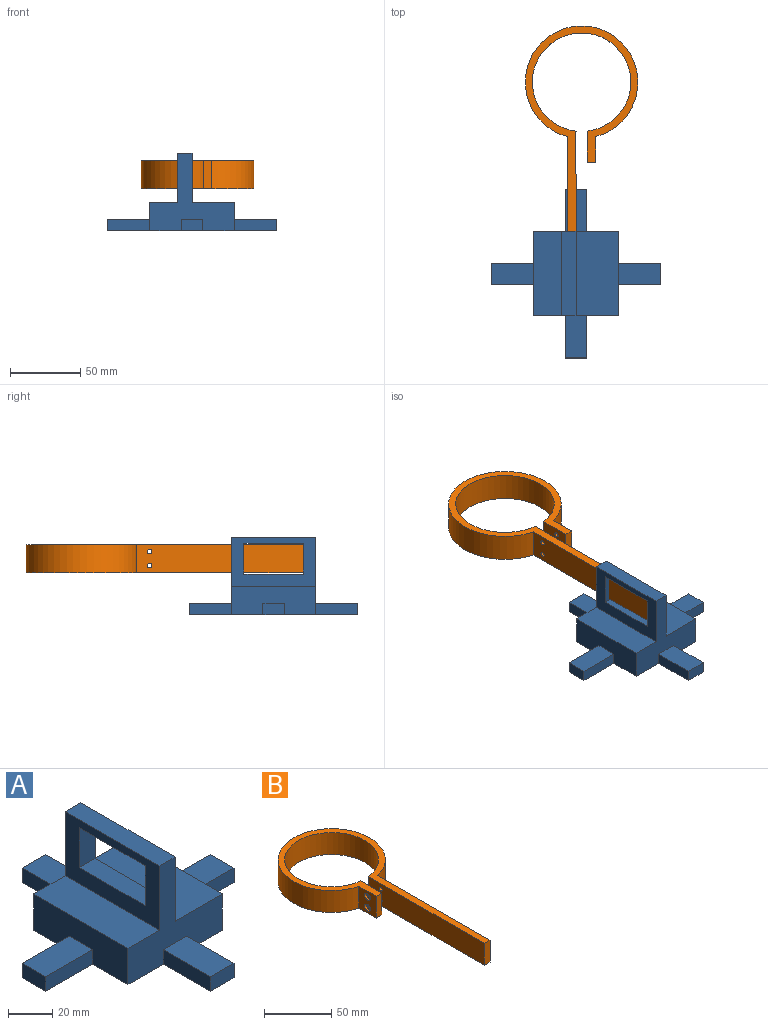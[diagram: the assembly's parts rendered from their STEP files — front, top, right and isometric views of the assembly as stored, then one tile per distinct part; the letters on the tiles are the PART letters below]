
ASSEMBLY  parts=2 mates=1
PART A: 30 faces, bbox 120x120x55.3 mm
  f0: plane 60x35.32mm, normal (-1,0,0), area 1195.5mm2, adj f4,f5,f7,f25,f26,f27,f28,f29
  f1: plane 60x35.32mm, normal (1,0,0), area 1195.5mm2, adj f2,f4,f5,f25,f26,f27,f28,f29
  f2: plane 60x30mm, normal (0,0,1), area 1800mm2, adj f1,f4,f5,f6
  f3: plane 60x20mm, normal (-1,0,0), area 1080mm2, adj f4,f5,f7,f8,f21,f23,f24
  f4: plane 60x55.32mm, normal (0,1,0), area 1433.2mm2, adj f0,f1,f2,f3,f6,f7,f8,f9
  f5: plane 60x55.32mm, normal (0,-1,0), area 1433.2mm2, adj f0,f1,f2,f3,f6,f7,f8,f13
  f6: plane 60x20mm, normal (1,0,0), area 1080mm2, adj f2,f4,f5,f8,f17,f18,f20
  f7: plane 60x20mm, normal (0,0,1), area 1200mm2, adj f0,f3,f4,f5
  f8: plane 120x120mm, normal (0,0,-1), area 5400mm2, adj f3,f4,f5,f6,f9,f10,f11,f13
  f9: plane 30x8mm, normal (-1,0,0), area 240mm2, adj f4,f8,f11,f12
  f10: plane 30x8mm, normal (1,0,0), area 240mm2, adj f4,f8,f11,f12
  f11: plane 15x8mm, normal (0,1,0), area 120mm2, adj f8,f9,f10,f12
  f12: plane 30x15mm, normal (0,0,1), area 450mm2, adj f4,f9,f10,f11
  f13: plane 30x8mm, normal (1,0,0), area 240mm2, adj f5,f8,f15,f16
  f14: plane 30x8mm, normal (-1,0,0), area 240mm2, adj f5,f8,f15,f16
  f15: plane 15x8mm, normal (0,-1,0), area 120mm2, adj f8,f13,f14,f16
  f16: plane 30x15mm, normal (0,0,1), area 450mm2, adj f5,f13,f14,f15
  f17: plane 30x8mm, normal (0,1,0), area 240mm2, adj f6,f8,f19,f20
  f18: plane 30x8mm, normal (0,-1,0), area 240mm2, adj f6,f8,f19,f20
  f19: plane 15x8mm, normal (1,0,0), area 120mm2, adj f8,f17,f18,f20
  f20: plane 30x15mm, normal (0,0,1), area 450mm2, adj f6,f17,f18,f19
  f21: plane 30x8mm, normal (0,1,0), area 240mm2, adj f3,f8,f22,f24
  f22: plane 15x8mm, normal (-1,0,0), area 120mm2, adj f8,f21,f23,f24
  f23: plane 30x8mm, normal (0,-1,0), area 240mm2, adj f3,f8,f22,f24
  f24: plane 30x15mm, normal (0,0,1), area 450mm2, adj f3,f21,f22,f23
  f25: plane 42x10mm, normal (0,0,1), area 420mm2, adj f0,f1,f26,f28
  f26: plane 22x10mm, normal (0,-1,0), area 220mm2, adj f0,f1,f25,f27
  f27: plane 42x10mm, normal (0,0,-1), area 420mm2, adj f0,f1,f26,f28
  f28: plane 22x10mm, normal (0,1,0), area 220mm2, adj f0,f1,f25,f27
  f29: plane 60x10mm, normal (0,0,1), area 600mm2, adj f0,f1,f4,f5
PART B: 20 faces, bbox 80x197x20 mm
  f0: cylinder r=40mm len=80mm, axis (0,0,-1), area 4622.3mm2, adj f1,f8,f9,f10
  f1: plane 20x18.27mm, normal (-1,0,0), area 308.9mm2, adj f0,f2,f9,f10,f14,f18
  f2: plane 20x6mm, normal (0,-1,0), area 120mm2, adj f1,f3,f9,f10
  f3: plane 22x20mm, normal (1,0,0), area 423.9mm2, adj f2,f4,f9,f10,f12,f16
  f4: plane 20x0.25mm, normal (0.82,0.58,0), area 6.1mm2, adj f3,f5,f9,f10
  f5: cylinder r=35mm len=70mm, axis (0,0,-1), area 4235.8mm2, adj f4,f6,f9,f10
  f6: plane 20x0.22mm, normal (-0.95,-0.32,0), area 4.7mm2, adj f5,f7,f9,f10
  f7: plane 122x20mm, normal (-1,0,0), area 2423.9mm2, adj f6,f9,f10,f11,f15,f19
  f8: plane 118.27x20mm, normal (1,0,0), area 2349.3mm2, adj f0,f9,f10,f11,f15,f19
  f9: plane 197x80mm, normal (0,0,1), area 1949.9mm2, adj f0,f1,f2,f3,f4,f5,f6,f7
  f10: plane 197x80mm, normal (0,0,-1), area 1949.9mm2, adj f0,f1,f2,f3,f4,f5,f6,f7
  f11: cylinder r=1.6mm len=6mm, axis (-1,0,0), area 60.3mm2, adj f7,f8
  f12: cylinder r=1.6mm len=4mm, axis (-1,0,0), area 40.2mm2, adj f3,f13
  f13: plane 6x6mm, normal (-1,0,0), area 20.2mm2, adj f12,f14
  f14: cylinder r=3mm len=6mm, axis (-1,0,0), area 37.7mm2, adj f1,f13
  f15: cylinder r=1.6mm len=6mm, axis (-1,0,0), area 60.3mm2, adj f7,f8
  f16: cylinder r=1.6mm len=4mm, axis (-1,0,0), area 40.2mm2, adj f3,f17
  f17: plane 6x6mm, normal (-1,0,0), area 20.2mm2, adj f16,f18
  f18: cylinder r=3mm len=6mm, axis (-1,0,0), area 37.7mm2, adj f1,f17
  f19: plane 20x6mm, normal (0,-1,0), area 120mm2, adj f7,f8,f9,f10
PLACE A t=(-18.31,2.53,4.3)mm
PLACE B rot(axis=(0,-1,0),180deg) t=(-14.31,88.53,54.3)mm
MATE revolute B.f7 <-> A.f1  axis (1,0,0) through (-18.31,-18.47,44.3)mm
